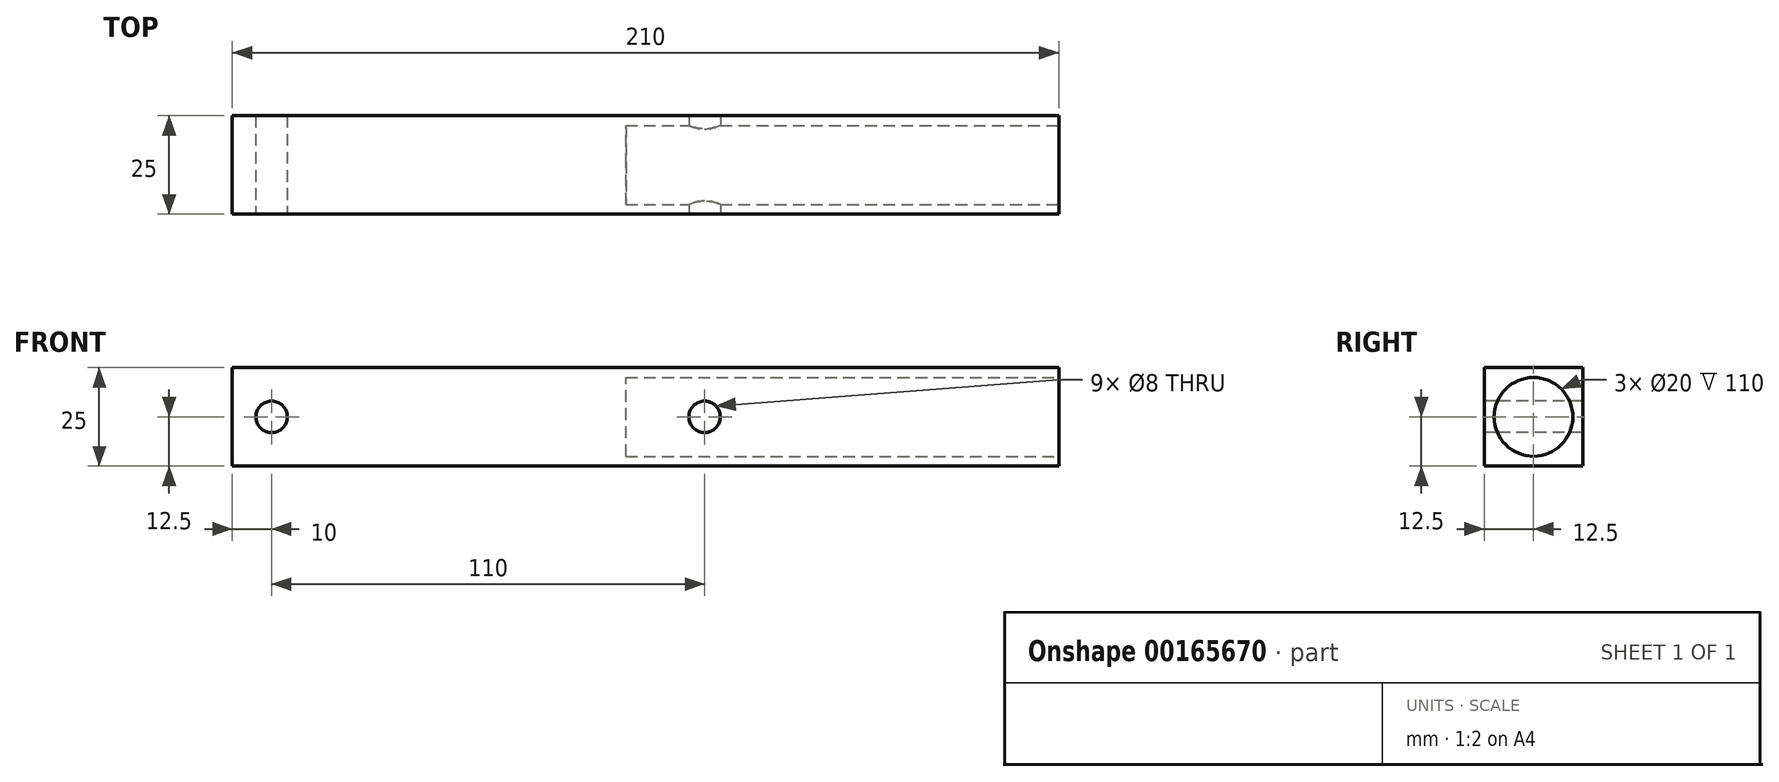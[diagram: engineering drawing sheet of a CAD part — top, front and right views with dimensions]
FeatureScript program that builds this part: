
annotation { "Feature Type Name" : "Feature", "Feature Type Description" : "" }
export const myFeature = defineFeature(function(context is Context, id is Id, definition is map)
    precondition{}
    {
        {
            var Q0;
            Q0=qCreatedBy(makeId("Top.planeOp"),FACE);
            var sketch = newSketch(context, id + "F0", { "sketchPlane" : qUnion([Q0])});
            skLineSegment(sketch, "E0.bottom", {"start": v(105, -12.5) * mm, "end": v(-105, -12.5) * mm});
            skLineSegment(sketch, "E0.top", {"start": v(105, 12.5) * mm, "end": v(-105, 12.5) * mm});
            skLineSegment(sketch, "E0.left", {"start": v(105, -12.5) * mm, "end": v(105, 12.5) * mm});
            skLineSegment(sketch, "E0.right", {"start": v(-105, -12.5) * mm, "end": v(-105, 12.5) * mm});
            skPoint(sketch, "E0.middle", {"position": v(0, 0) * mm});
            skSolve(sketch);
        }
        {
            var Q0;
            Q0=makeQuery(id+"F0.imprint","IMPRINT",FACE,{"disambiguationData":[TD([[makeQuery(id+"F0.imprint","IMPRINT",EDGE,{"derivedFrom":sQuery(id+"F0.wireOp",EDGE,"E0.bottom")}),-1.0]])]});
            extrude(context, id + "F1", {"entities" : qUnion([Q0]), "depth" : 25 * mm, "offsetDistance" : 25 * mm});
        }
        {
            var Q0;
            Q0=makeQuery(id+"F1.opExtrude","SWEPT_FACE",FACE,{"disambiguationData":[OSD([sQuery(id+"F0.wireOp",EDGE,"E0.bottom")])]});
            var sketch = newSketch(context, id + "F2", { "sketchPlane" : qUnion([Q0])});
            skCircle(sketch, "E1", {"center": v(-95, 12.5) * mm, "radius": 4 * mm});
            skPoint(sketch, "E1.centerSnap0", {"position": v(-105, 12.5) * mm});
            skCircle(sketch, "E2", {"center": v(15, 12.5) * mm, "radius": 4 * mm});
            skSolve(sketch);
        }
        {
            var Q0;
            Q0=makeQuery(id+"F2.imprint","IMPRINT",FACE,{"disambiguationData":[TD([[makeQuery(id+"F2.imprint","IMPRINT",EDGE,{"derivedFrom":sQuery(id+"F2.wireOp",EDGE,"E1")}),1.0]])]});
            var Q1;
            Q1=makeQuery(id+"F2.imprint","IMPRINT",FACE,{"disambiguationData":[TD([[makeQuery(id+"F2.imprint","IMPRINT",EDGE,{"derivedFrom":sQuery(id+"F2.wireOp",EDGE,"E2")}),1.0]])]});
            extrude(context, id + "F3", {"entities" : qUnion([Q0, Q1]), "operationType" : NewBodyOperationType.REMOVE, "endBound" : BoundingType.THROUGH_ALL, "oppositeDirection" : true, "depth" : 25 * mm, "offsetDistance" : 25 * mm});
        }
        {
            var Q0;
            Q0=makeQuery(id+"F1.opExtrude","SWEPT_FACE",FACE,{"disambiguationData":[OSD([sQuery(id+"F0.wireOp",EDGE,"E0.left")])]});
            var sketch = newSketch(context, id + "F4", { "sketchPlane" : qUnion([Q0])});
            skCircle(sketch, "E3", {"center": v(0, 12.5) * mm, "radius": 10 * mm});
            skPoint(sketch, "E3.centerSnap0", {"position": v(12.5, 12.5) * mm});
            skSolve(sketch);
        }
        {
            var Q0;
            Q0=makeQuery(id+"F4.imprint","IMPRINT",FACE,{"disambiguationData":[TD([[makeQuery(id+"F4.imprint","IMPRINT",EDGE,{"derivedFrom":sQuery(id+"F4.wireOp",EDGE,"E3")}),1.0]])]});
            extrude(context, id + "F5", {"entities" : qUnion([Q0]), "operationType" : NewBodyOperationType.REMOVE, "oppositeDirection" : true, "depth" : 110 * mm, "offsetDistance" : 25 * mm});
        }
    });
